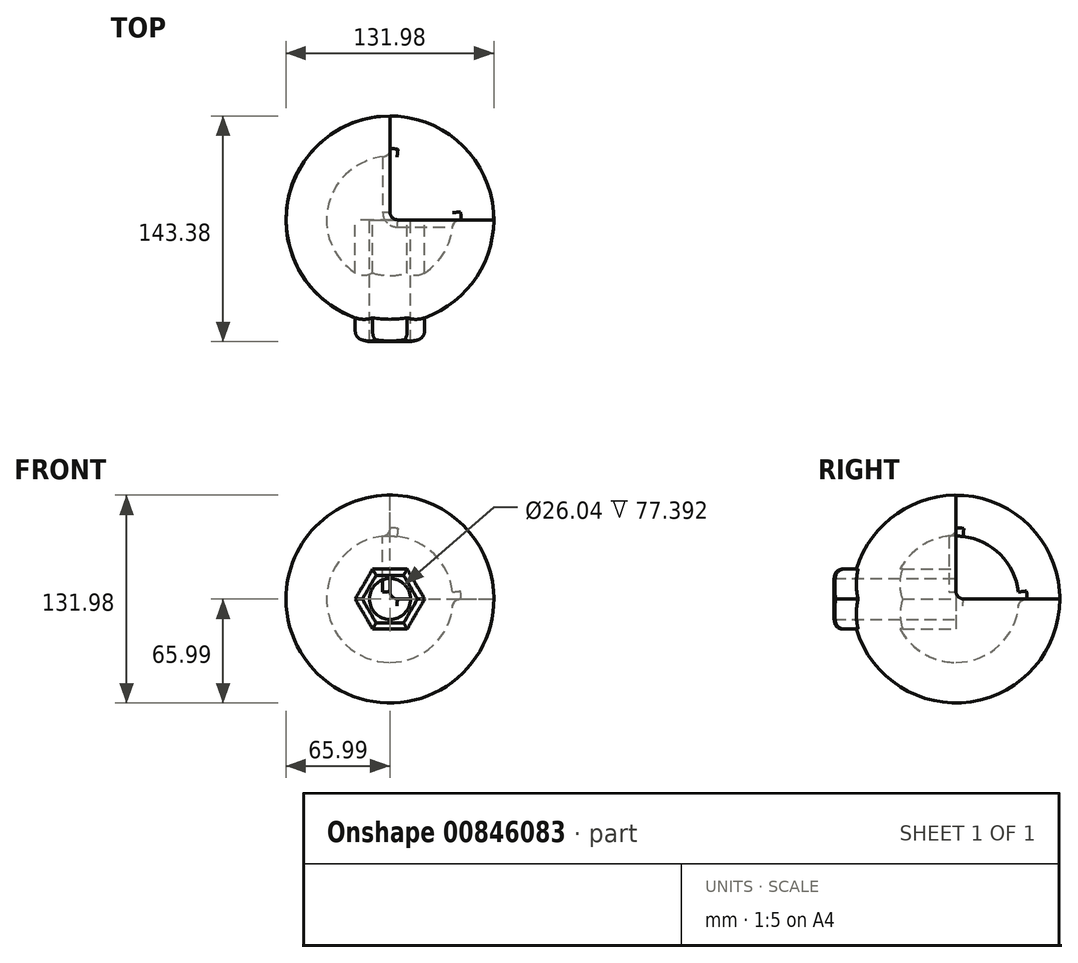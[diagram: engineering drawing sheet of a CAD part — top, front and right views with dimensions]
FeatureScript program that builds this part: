
annotation { "Feature Type Name" : "Feature", "Feature Type Description" : "" }
export const myFeature = defineFeature(function(context is Context, id is Id, definition is map)
    precondition{}
    {
        {
            var Q0;
            Q0=qCreatedBy(makeId("Top.planeOp"),FACE);
            var sketch = newSketch(context, id + "F0", { "sketchPlane" : qUnion([Q0])});
            skArc(sketch, "E0", {"start": v(0, -65.99) * mm, "mid": v(65.99, 0) * mm, "end": v(0, 65.99) * mm});
            skLineSegment(sketch, "E1", {"start": v(0, 65.99) * mm, "end": v(0, -65.99) * mm});
            skSolve(sketch);
        }
        {
            var Q0;
            Q0 = qSketchRegion(id + "F0", true);
            var Q1;
            Q1=sQuery(id+"F0.wireOp",EDGE,"E1");
            revolve(context, id + "F1", {"surfaceOperationType" : NewSurfaceOperationType.NEW, "entities" : qUnion([Q0]), "axis" : qUnion([Q1]), "revolveType" : RevolveType.FULL});
        }
        {
            var Q0;
            Q0=qCreatedBy(makeId("Front.planeOp"),FACE);
            var sketch = newSketch(context, id + "F2", { "sketchPlane" : qUnion([Q0])});
            skLineSegment(sketch, "E2.bottom", {"start": v(0, 0) * mm, "end": v(82.94, 0) * mm});
            skLineSegment(sketch, "E2.top", {"start": v(0, 76) * mm, "end": v(82.94, 76) * mm});
            skLineSegment(sketch, "E2.left", {"start": v(0, 0) * mm, "end": v(0, 76) * mm});
            skLineSegment(sketch, "E2.right", {"start": v(82.94, 0) * mm, "end": v(82.94, 76) * mm});
            skSolve(sketch);
        }
        {
            var Q0;
            Q0 = qSketchRegion(id + "F2", true);
            extrude(context, id + "F3", {"entities" : qUnion([Q0]), "operationType" : NewBodyOperationType.REMOVE, "oppositeDirection" : true, "depth" : 68.58 * mm, "offsetDistance" : 25.4 * mm});
        }
        {
            var Q0;
            Q0=makeQuery(id+"F3.boolean.opBoolean","COPY",EDGE,{"derivedFrom":makeQuery(id+"F3.opExtrude","CAP_EDGE",EDGE,{"disambiguationData":[OSD([sQuery(id+"F2.wireOp",EDGE,"E2.bottom")])],"isStart":true})});
            var Q1;
            Q1=makeQuery(id+"F3.boolean.opBoolean","COPY",EDGE,{"derivedFrom":makeQuery(id+"F3.opExtrude","CAP_EDGE",EDGE,{"disambiguationData":[OSD([sQuery(id+"F2.wireOp",EDGE,"E2.left")])],"isStart":true})});
            var Q2;
            Q2=makeQuery(id+"F3.boolean.opBoolean","COPY",EDGE,{"derivedFrom":makeQuery(id+"F3.opExtrude","SWEPT_EDGE",EDGE,{"disambiguationData":[OSD([sQuery(id+"F2.wireOp",EDGE,"E2.bottom"),sQuery(id+"F2.wireOp",EDGE,"E2.left")])]})});
            fillet(context, id + "F4", {"entities" : qUnion([Q0, Q1, Q2]), "radius" : 5.08 * mm, "tangentPropagation" : true, "allowEdgeOverflow" : false});
        }
        {
            var Q0;
            Q0=qCreatedBy(makeId("Right.planeOp"),FACE);
            var sketch = newSketch(context, id + "F5", { "sketchPlane" : qUnion([Q0])});
            skArc(sketch, "E3", {"start": v(0, -40.25) * mm, "mid": v(40.25, 0) * mm, "end": v(0, 40.25) * mm});
            skLineSegment(sketch, "E4", {"start": v(0, 40.25) * mm, "end": v(0, -40.25) * mm});
            skPoint(sketch, "E5.orphan", {"position": v(0, 49.04) * mm});
            skSolve(sketch);
        }
        {
            var Q0;
            Q0=makeQuery(id+"F5.imprint","IMPRINT",FACE,{"disambiguationData":[TD([[makeQuery(id+"F5.imprint","IMPRINT",EDGE,{"derivedFrom":sQuery(id+"F5.wireOp",EDGE,"E3")}),1.0]])]});
            var Q1;
            Q1=sQuery(id+"F5.wireOp",EDGE,"E4");
            revolve(context, id + "F6", {"operationType" : NewBodyOperationType.REMOVE, "surfaceOperationType" : NewSurfaceOperationType.NEW, "entities" : qUnion([Q0]), "axis" : qUnion([Q1]), "revolveType" : RevolveType.FULL, "oppositeDirection" : true});
        }
        {
            var Q0;
            Q0=makeQuery(id+"F6.boolean.opBoolean","INTERSECT",EDGE,{"derivedFrom":[makeQuery(id+"F3.boolean.opBoolean","COPY",FACE,{"derivedFrom":makeQuery(id+"F3.opExtrude","SWEPT_FACE",FACE,{"disambiguationData":[OSD([sQuery(id+"F2.wireOp",EDGE,"E2.bottom")])]})}),makeQuery(id+"F6.opRevolve","SWEPT_FACE",FACE,{"disambiguationData":[OSD([sQuery(id+"F5.wireOp",EDGE,"E3")])]})]});
            fillet(context, id + "F7", {"entities" : qUnion([Q0]), "radius" : 5.08 * mm, "tangentPropagation" : true, "allowEdgeOverflow" : false});
        }
        {
            var Q0;
            Q0=qCreatedBy(makeId("Front.planeOp"),FACE);
            var sketch = newSketch(context, id + "F8", { "sketchPlane" : qUnion([Q0])});
            skCircle(sketch, "E6.cCircle", {"center": v(0, 0) * mm, "radius": 19.05 * mm, "construction": true});
            skLineSegment(sketch, "E6.0", {"start": v(-11, 19.05) * mm, "end": v(11, 19.05) * mm});
            skLineSegment(sketch, "E6.1", {"start": v(11, 19.05) * mm, "end": v(22, 0) * mm});
            skLineSegment(sketch, "E6.2", {"start": v(22, 0) * mm, "end": v(11, -19.05) * mm});
            skLineSegment(sketch, "E6.3", {"start": v(11, -19.05) * mm, "end": v(-11, -19.05) * mm});
            skLineSegment(sketch, "E6.4", {"start": v(-11, -19.05) * mm, "end": v(-22, 0) * mm});
            skLineSegment(sketch, "E6.5", {"start": v(-22, 0) * mm, "end": v(-11, 19.05) * mm});
            skPoint(sketch, "E6.0.midPoint", {"position": v(0, 19.05) * mm});
            skSolve(sketch);
        }
        {
            var Q0;
            Q0 = qSketchRegion(id + "F8", true);
            var Q1;
            Q1=makeQuery(id+"F1.opRevolve","SWEPT_FACE",FACE,{"disambiguationData":[OSD([sQuery(id+"F0.wireOp",EDGE,"E0")])]});
            extrude(context, id + "F9", {"entities" : qUnion([Q0]), "operationType" : NewBodyOperationType.ADD, "endBound" : BoundingType.UP_TO_SURFACE, "depth" : 25.4 * mm, "endBoundEntityFace" : qUnion([Q1]), "hasOffset" : true, "offsetDistance" : 12.7 * mm, "offsetOppositeDirection" : true});
        }
        {
            var Q0;
            Q0=makeQuery(id+"F9.opExtrude","CAP_EDGE",EDGE,{"disambiguationData":[OSD([sQuery(id+"F8.wireOp",EDGE,"E6.2")])],"isStart":false});
            var Q1;
            Q1=makeQuery(id+"F9.opExtrude","CAP_EDGE",EDGE,{"disambiguationData":[OSD([sQuery(id+"F8.wireOp",EDGE,"E6.3")])],"isStart":false});
            var Q2;
            Q2=makeQuery(id+"F9.opExtrude","CAP_EDGE",EDGE,{"disambiguationData":[OSD([sQuery(id+"F8.wireOp",EDGE,"E6.4")])],"isStart":false});
            var Q3;
            Q3=makeQuery(id+"F9.opExtrude","CAP_EDGE",EDGE,{"disambiguationData":[OSD([sQuery(id+"F8.wireOp",EDGE,"E6.5")])],"isStart":false});
            var Q4;
            Q4=makeQuery(id+"F9.opExtrude","CAP_EDGE",EDGE,{"disambiguationData":[OSD([sQuery(id+"F8.wireOp",EDGE,"E6.0")])],"isStart":false});
            var Q5;
            Q5=makeQuery(id+"F9.opExtrude","CAP_EDGE",EDGE,{"disambiguationData":[OSD([sQuery(id+"F8.wireOp",EDGE,"E6.1")])],"isStart":false});
            fillet(context, id + "F10", {"entities" : qUnion([Q0, Q1, Q2, Q3, Q4, Q5]), "radius" : 5.08 * mm, "tangentPropagation" : true, "allowEdgeOverflow" : false});
        }
        {
            var Q0;
            Q0=makeQuery(id+"F9.opExtrude","CAP_FACE",FACE,{"disambiguationData":[OSD([sQuery(id+"F8.wireOp",EDGE,"E6.0"),sQuery(id+"F8.wireOp",EDGE,"E6.1"),sQuery(id+"F8.wireOp",EDGE,"E6.2"),sQuery(id+"F8.wireOp",EDGE,"E6.3"),sQuery(id+"F8.wireOp",EDGE,"E6.4"),sQuery(id+"F8.wireOp",EDGE,"E6.5")])],"isStart":true});
            var sketch = newSketch(context, id + "F11", { "sketchPlane" : qUnion([Q0])});
            skCircle(sketch, "E7", {"center": v(0, 0) * mm, "radius": 13.02 * mm});
            skSolve(sketch);
        }
        {
            var Q0;
            Q0 = qSketchRegion(id + "F11", true);
            extrude(context, id + "F12", {"entities" : qUnion([Q0]), "operationType" : NewBodyOperationType.REMOVE, "oppositeDirection" : true, "depth" : 86.36 * mm, "offsetDistance" : 25.4 * mm});
        }
    });
